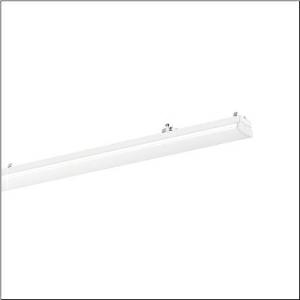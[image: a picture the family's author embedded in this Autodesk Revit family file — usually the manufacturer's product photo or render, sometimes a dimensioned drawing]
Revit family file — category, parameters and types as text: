
# Revit family: licross_r__21_recessed_opal_ho_52te1dcn4cxm_2120
name_source: partatom
category: Lighting Fixtures
units: mm (PartAtom-declared; Revit-internal decimal feet)

## family parameters
Cut with Voids When Loaded = No
Host = Face
Light Source = No
Part Type = Normal
Room Calculation Point = No
Round Connector Dimension = Use Diameter
Shared = No

## types (1)
- --- (1 x LED, 12300 lm, 68.4 W, 4000K)
    Apparent Load = 68 VA
    CIE Flux Codes = 44 73 91 87 100
    Color Rendering = 80
    Color Temperature = 4000K
    Default Elevation = 1800 mm
    Description = Licross® 21 recessed opal HO, luminaire insert, of sheet steel, galvanised, coil coated, white, length: 1.500mm, width: 66mm, height: 67mm, LED rated luminous flux: 12.300lm, light colour: 840, control gear: ON/OFF Multilumen, CLOi, with plug, 3-pole, with phase selection, mains connection: 220..240V, AC, 50/60Hz, start of lifetime: 68W, end of service life: 83W, halogen-free wiring, primary optical cover: cover, of PMMA, light emission: direct with ceiling illumination distribution, primary light characteristic: symmetric, protection rating (complete): IP54, insulation class (complete): insulation class I (protective earthing), certification: CE, ENEC, VDE, UKCA, protection symbol: D if used in an environment with non-conductive dust loads with corresponding accessories, impact resistance: IK06, permissible ambient temperature for indoor applications: -35..+30°C, corresponds to IFS (International Featured Standards) requirements for safety and quality in the food industry, reducing of maximum allowable ambient temperature of 5°C with ceiling mounting, LABS conformity tested according to VDMA 24364:2018-05, packaging unit: 1 piece
    Height = 83 mm
    Lamp = 1 x LED
    Lamp Light Flux = 12300 lm
    Lamp Power = 68.4 W
    Lamp count = 1
    Length = 1500 mm
    Luminous efficacy = 180 lm/W
    Manufacturer = Siteco
    ModVariant = No
    Model = 52TE1DCN4CXM
    Mounting Place = Ceiling
    Mounting Type = Pendant
    Number of Poles = 1
    OnlyDefault = Yes
    Power Factor = 1
    Product Name = Licross® 21 recessed opal HO
    Product group = luminaire insert
    ProductGroupID = 902
    Protection Class = Protection class I
    Protection Degree = IP 54
    RLX_Detail_Level = 1
    RLX_Emergency_Light_Flux = 0 lm
    RLX_Emergency_Type = 0
    RLX_Emergency_Type_DB = No
    RlxData = <blob elided: 24725 chars, md5=e05640a7>
    Socket = socket
    Standby Power = 0 W
    System Light Flux = 12300 lm
    System Power = 68 W
    Type Comments = factory setting: luminous flux: 100 % | (A | C | E) | 161 mA
    Type Image = l_1313666.jpg
    URL = http://relux.com
    VarID = @adj_068506
    Voltage = 0 V
    Weight = 0.00 kg
    Width = 76 mm

## geometry (parser evidence)
native form markers: Blend x4, Sweep x13
no freeform markers — native parametric forms only
